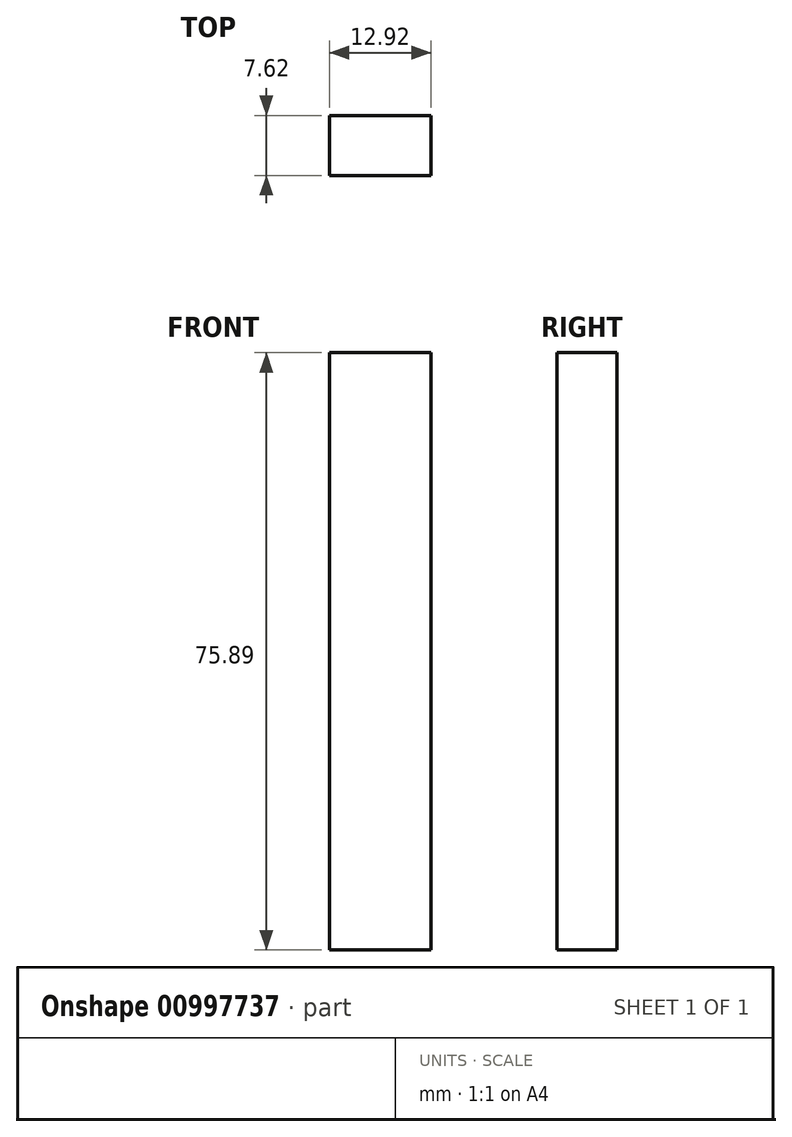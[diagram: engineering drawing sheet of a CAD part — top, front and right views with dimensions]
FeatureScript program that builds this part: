
annotation { "Feature Type Name" : "Feature", "Feature Type Description" : "" }
export const myFeature = defineFeature(function(context is Context, id is Id, definition is map)
    precondition{}
    {
        {
            var Q0;
            Q0=qCreatedBy(makeId("Front.planeOp"),FACE);
            var sketch = newSketch(context, id + "F0", { "sketchPlane" : qUnion([Q0])});
            skLineSegment(sketch, "E0.bottom", {"start": v(-33.63, 74.5) * mm, "end": v(-20.71, 74.5) * mm});
            skLineSegment(sketch, "E0.top", {"start": v(-33.63, -1.4) * mm, "end": v(-20.71, -1.4) * mm});
            skLineSegment(sketch, "E0.left", {"start": v(-33.63, 74.5) * mm, "end": v(-33.63, -1.4) * mm});
            skLineSegment(sketch, "E0.right", {"start": v(-20.71, 74.5) * mm, "end": v(-20.71, -1.4) * mm});
            skSolve(sketch);
        }
        {
            var Q0;
            Q0=makeQuery(id+"F0.imprint","IMPRINT",FACE,{"disambiguationData":[TD([[makeQuery(id+"F0.imprint","IMPRINT",EDGE,{"derivedFrom":sQuery(id+"F0.wireOp",EDGE,"E0.bottom")}),-1.0]])]});
            extrude(context, id + "F1", {"entities" : qUnion([Q0]), "depth" : 7.62 * mm, "offsetDistance" : 25.4 * mm});
        }
    });
